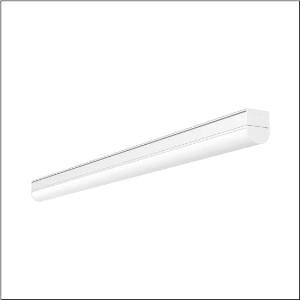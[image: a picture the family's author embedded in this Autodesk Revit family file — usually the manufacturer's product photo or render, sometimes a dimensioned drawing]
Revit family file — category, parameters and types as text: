
# Revit family: ecopack_r__31_51lj12dnm80a_c0ee
name_source: partatom
category: Lighting Fixtures
units: mm (PartAtom-declared; Revit-internal decimal feet)

## family parameters
Cut with Voids When Loaded = No
Host = Face
Light Source = No
Part Type = Normal
Room Calculation Point = No
Round Connector Dimension = Use Diameter
Shared = No

## types (1)
- --- (1 x LED, 6780 lm, 52 W, 5000K)
    Apparent Load = 52 VA
    CIE Flux Codes = 39 67 87 89 100
    Color Rendering = 80
    Color Temperature = 5000K
    Default Elevation = 1800 mm
    Description = Ecopack® 31, diffuser luminaire, primary optical cover: cover, of PC, frosted, light emission: direct distribution, primary light characteristic: symmetric, installation type: surface-mounted, LED, rated luminous flux: 7.000lm, luminous efficacy: 135lm/W, light colour: 830/840/850, colour temperature: 3000/4000/5000K, control gear: ECG DALI, with terminal, 5-pole, mains connection: 220..240V, AC, 50/60Hz, rated input power: 52W, housing, of aluminium, traffic white (RAL 9016), length: 1.450mm, width: 56mm, height: 68mm, end cap, of PC, white, protection rating (complete): IP20, insulation class (complete): insulation class I (protective earthing), certification: CE, impact resistance: IK06, permissible operating ambient temperature: -20..+40°C, packaging unit: 1 piece
    Height = 68 mm
    Lamp = 1 x LED
    Lamp Light Flux = 6780 lm
    Lamp Power = 52 W
    Lamp count = 1
    Length = 1450 mm
    Luminous efficacy = 130 lm/W
    Manufacturer = Siteco
    ModVariant = No
    Model = 51LJ12DNM80A
    Mounting Place = Ceiling
    Mounting Type = Surface mounted
    Number of Poles = 1
    OnlyDefault = Yes
    Power Factor = 1
    Product Name = Ecopack® 31
    Product group = diffuser luminaire
    ProductGroupID = 303
    Protection Class = Protection class I
    Protection Degree = IP 20
    RLX_Detail_Level = 1
    RLX_Emergency_Light_Flux = 0 lm
    RLX_Emergency_Type = 0
    RLX_Emergency_Type_DB = No
    RlxData = <blob elided: 21625 chars, md5=a5234cf4>
    Socket = socket
    Standby Power = 0 W
    System Light Flux = 6780 lm
    System Power = 52 W
    Type Comments = individual setting: colour temperature 5000K
    Type Image = l_1007033.jpg
    URL = http://relux.com
    VarID = @adj_107019
    Voltage = 0 V
    Weight = 0.00 kg
    Width = 56 mm

## geometry (parser evidence)
native form markers: Blend x4, Sweep x11
no freeform markers — native parametric forms only
